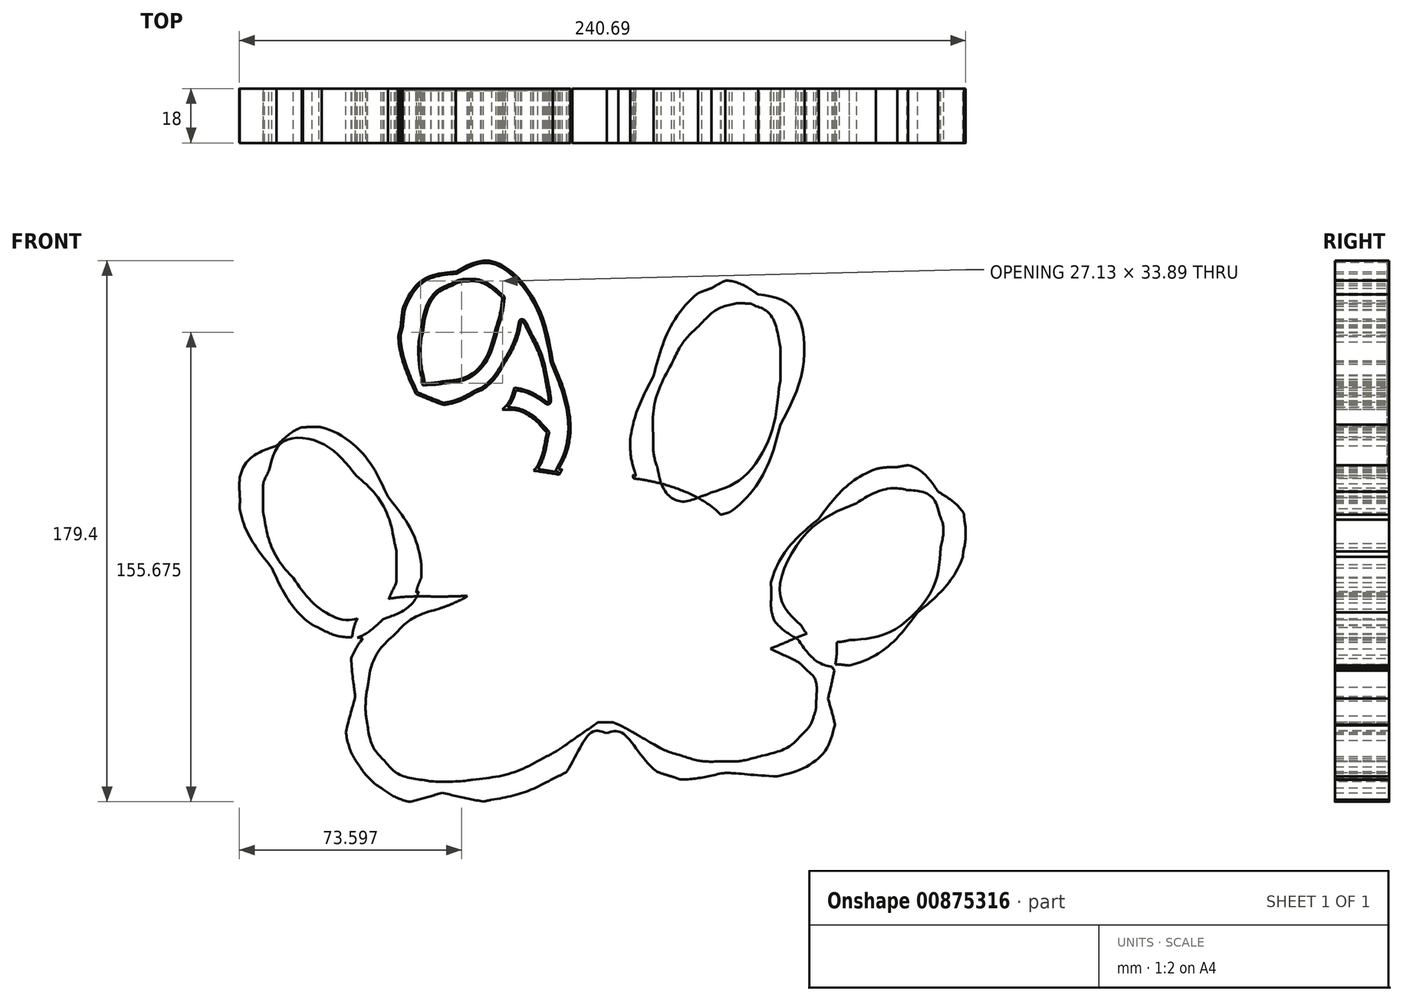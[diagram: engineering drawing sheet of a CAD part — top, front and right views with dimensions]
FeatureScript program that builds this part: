
annotation { "Feature Type Name" : "Feature", "Feature Type Description" : "" }
export const myFeature = defineFeature(function(context is Context, id is Id, definition is map)
    precondition{}
    {
        {
            var Q0;
            Q0=qCreatedBy(makeId("Front.planeOp"),FACE);
            var sketch = newSketch(context, id + "F0", { "sketchPlane" : qUnion([Q0])});
            skLineSegment(sketch, "E0", {"start": v(-80.3, -36.83) * mm, "end": v(-79.54, -35.55) * mm});
            skLineSegment(sketch, "E1", {"start": v(-79.54, -35.55) * mm, "end": v(-82.14, -35.4) * mm});
            skLineSegment(sketch, "E2", {"start": v(-13.99, 21.5) * mm, "end": v(-14.63, 20.22) * mm});
            skLineSegment(sketch, "E3", {"start": v(-14.63, 20.22) * mm, "end": v(-12.85, 20.36) * mm});
            skLineSegment(sketch, "E4", {"start": v(78.32, -44.34) * mm, "end": v(75.75, -44.48) * mm});
            skLineSegment(sketch, "E5", {"start": v(75.75, -44.48) * mm, "end": v(76.38, -45.72) * mm});
            skLineSegment(sketch, "E6", {"start": v(2.33, -71.3) * mm, "end": v(1.37, -70.89) * mm});
            skLineSegment(sketch, "E7", {"start": v(1.37, -70.89) * mm, "end": v(0.6, -71.36) * mm});
            skLineSegment(sketch, "E8", {"start": v(-18.9, 30.27) * mm, "end": v(-18.36, 32.47) * mm});
            skLineSegment(sketch, "E9", {"start": v(-18.36, 32.47) * mm, "end": v(-19.73, 33.87) * mm});
            skLineSegment(sketch, "E10", {"start": v(-59.45, 51.7) * mm, "end": v(-58.94, 48.84) * mm});
            skLineSegment(sketch, "E11", {"start": v(-58.94, 48.84) * mm, "end": v(-56.82, 48.98) * mm});
            skFitSpline(sketch, "E12", {"points": [v(-15.34, 34.63) * mm, v(-18.4, 39.06) * mm, v(-30.81, 48.02) * mm, v(-39.96, 41.9) * mm]});
            skFitSpline(sketch, "E13", {"points": [v(-39.96, 41.9) * mm, v(-49.1, 35.76) * mm, v(-49.72, 24.31) * mm, v(-47.56, 20.99) * mm]});
            skFitSpline(sketch, "E14", {"points": [v(-61.86, 45.3) * mm, v(-31.13, 42.45) * mm, v(-29.4, 77.45) * mm, v(-29.37, 77.9) * mm, v(-29.37, 77.9) * mm, v(-29.37, 77.91) * mm]});
            skFitSpline(sketch, "E15", {"points": [v(-48.61, 85.84) * mm, v(-60.56, 82.37) * mm, v(-67.65, 65.27) * mm, v(-61.86, 45.3) * mm]});
            skFitSpline(sketch, "E16", {"points": [v(-61.86, 45.3) * mm, v(-56.07, 25.33) * mm, v(-39.6, 10.07) * mm, v(-27.64, 13.53) * mm]});
            skFitSpline(sketch, "E17", {"points": [v(-27.64, 13.53) * mm, v(-15.69, 17) * mm, v(-10.7, 36) * mm, v(-16.48, 55.96) * mm]});
            skFitSpline(sketch, "E18", {"points": [v(-16.48, 55.96) * mm, v(-22.28, 75.93) * mm, v(-36.66, 89.3) * mm, v(-48.61, 85.84) * mm]});
            skFitSpline(sketch, "E19", {"points": [v(51.53, 78.32) * mm, v(39.92, 82.8) * mm, v(24.43, 70.73) * mm, v(16.93, 51.34) * mm]});
            skFitSpline(sketch, "E20", {"points": [v(16.93, 51.34) * mm, v(9.43, 31.95) * mm, v(12.76, 12.6) * mm, v(24.36, 8.1) * mm]});
            skFitSpline(sketch, "E21", {"points": [v(24.36, 8.1) * mm, v(35.97, 3.61) * mm, v(51.46, 15.7) * mm, v(58.96, 35.08) * mm]});
            skFitSpline(sketch, "E22", {"points": [v(58.96, 35.08) * mm, v(66.46, 54.47) * mm, v(63.13, 73.83) * mm, v(51.53, 78.32) * mm]});
            skFitSpline(sketch, "E23", {"points": [v(-108.03, 28.18) * mm, v(-118.63, 21.67) * mm, v(-119.33, 3.52) * mm, v(-109.59, -12.37) * mm]});
            skFitSpline(sketch, "E24", {"points": [v(-109.59, -12.37) * mm, v(-99.84, -28.26) * mm, v(-83.34, -35.86) * mm, v(-72.73, -29.35) * mm]});
            skFitSpline(sketch, "E25", {"points": [v(-72.73, -29.35) * mm, v(-62.12, -22.84) * mm, v(-61.42, -4.69) * mm, v(-71.17, 11.2) * mm]});
            skFitSpline(sketch, "E26", {"points": [v(-71.17, 11.2) * mm, v(-80.92, 27.09) * mm, v(-97.42, 34.69) * mm, v(-108.03, 28.18) * mm]});
            skFitSpline(sketch, "E27", {"points": [v(111.2, 12.89) * mm, v(102.17, 21.45) * mm, v(84.46, 17.41) * mm, v(71.64, 3.88) * mm]});
            skFitSpline(sketch, "E28", {"points": [v(71.64, 3.88) * mm, v(58.83, -9.66) * mm, v(55.77, -27.56) * mm, v(64.8, -36.12) * mm]});
            skFitSpline(sketch, "E29", {"points": [v(64.8, -36.12) * mm, v(73.84, -44.68) * mm, v(91.55, -40.64) * mm, v(104.37, -27.1) * mm]});
            skFitSpline(sketch, "E30", {"points": [v(104.37, -27.1) * mm, v(117.18, -13.57) * mm, v(120.24, 4.33) * mm, v(111.2, 12.89) * mm]});
            skFitSpline(sketch, "E31", {"points": [v(-4.8, 16.91) * mm, v(13.08, 16.91) * mm, v(40.29, 3.9) * mm, v(43.89, -20.36) * mm]});
            skFitSpline(sketch, "E32", {"points": [v(43.89, -20.36) * mm, v(46.93, -40.9) * mm, v(74.7, -32.91) * mm, v(74.7, -55.73) * mm]});
            skFitSpline(sketch, "E33", {"points": [v(74.7, -55.73) * mm, v(74.7, -78.55) * mm, v(43.89, -80.46) * mm, v(39.32, -80.46) * mm]});
            skFitSpline(sketch, "E34", {"points": [v(39.32, -80.46) * mm, v(18.78, -80.46) * mm, v(6.61, -67.14) * mm, v(1.29, -67.14) * mm]});
            skFitSpline(sketch, "E35", {"points": [v(1.29, -67.14) * mm, v(-4.04, -67.14) * mm, v(-17.73, -86.92) * mm, v(-53.1, -86.92) * mm]});
            skFitSpline(sketch, "E36", {"points": [v(-53.1, -86.92) * mm, v(-85.93, -86.92) * mm, v(-82.06, -55.39) * mm, v(-82, -54.97) * mm, v(-82, -54.97) * mm, v(-82, -54.97) * mm]});
            skFitSpline(sketch, "E37", {"points": [v(-82, -54.97) * mm, v(-82, -54.97) * mm, v(-82, -54.97) * mm, v(-82, -54.64) * mm, v(-81.47, -29.6) * mm, v(-54.24, -21.88) * mm]});
            skFitSpline(sketch, "E38", {"points": [v(-54.24, -21.88) * mm, v(-31.42, -15.42) * mm, v(-51.58, 16.91) * mm, v(-4.8, 16.91) * mm]});
            skFitSpline(sketch, "E39", {"points": [v(-57.5, -90.51) * mm, v(-63.49, -89.98) * mm, v(-69.01, -88.15) * mm, v(-73.42, -85.24) * mm]});
            skFitSpline(sketch, "E40", {"points": [v(-73.42, -85.24) * mm, v(-75.42, -83.92) * mm, v(-78.97, -80.36) * mm, v(-80.36, -78.28) * mm]});
            skFitSpline(sketch, "E41", {"points": [v(-80.36, -78.28) * mm, v(-82.64, -74.86) * mm, v(-84.2, -71) * mm, v(-85.22, -66.2) * mm]});
            skFitSpline(sketch, "E42", {"points": [v(-85.22, -66.2) * mm, v(-85.75, -63.7) * mm, v(-85.79, -63.17) * mm, v(-85.78, -58.3) * mm]});
            skFitSpline(sketch, "E43", {"points": [v(-85.78, -58.3) * mm, v(-85.77, -53.92) * mm, v(-85.7, -52.66) * mm, v(-85.32, -50.6) * mm]});
            skFitSpline(sketch, "E44", {"points": [v(-85.32, -50.6) * mm, v(-84.46, -45.94) * mm, v(-82.46, -40.44) * mm, v(-80.3, -36.83) * mm]});
            skFitSpline(sketch, "E45", {"points": [v(-82.14, -35.4) * mm, v(-86.47, -35.16) * mm, v(-90.16, -34.16) * mm, v(-94.14, -32.14) * mm]});
            skFitSpline(sketch, "E46", {"points": [v(-94.14, -32.14) * mm, v(-102.91, -27.68) * mm, v(-110.59, -19.5) * mm, v(-115.4, -9.51) * mm]});
            skFitSpline(sketch, "E47", {"points": [v(-115.4, -9.51) * mm, v(-118.68, -2.68) * mm, v(-120.14, 3.3) * mm, v(-120.15, 10.04) * mm]});
            skFitSpline(sketch, "E48", {"points": [v(-120.15, 10.04) * mm, v(-120.17, 18.1) * mm, v(-118, 24.09) * mm, v(-113.44, 28.63) * mm]});
            skFitSpline(sketch, "E49", {"points": [v(-113.44, 28.63) * mm, v(-109.65, 32.4) * mm, v(-105.08, 34.21) * mm, v(-99.36, 34.2) * mm]});
            skFitSpline(sketch, "E50", {"points": [v(-99.36, 34.2) * mm, v(-92.65, 34.2) * mm, v(-85.88, 31.5) * mm, v(-79.3, 26.2) * mm]});
            skFitSpline(sketch, "E51", {"points": [v(-79.3, 26.2) * mm, v(-65.67, 15.24) * mm, v(-57.9, -4.22) * mm, v(-61.35, -18.7) * mm]});
            skFitSpline(sketch, "E52", {"points": [v(-61.35, -18.7) * mm, v(-61.57, -19.63) * mm, v(-61.73, -20.41) * mm, v(-61.7, -20.44) * mm]});
            skFitSpline(sketch, "E53", {"points": [v(-61.7, -20.44) * mm, v(-61.67, -20.47) * mm, v(-61.04, -20.25) * mm, v(-60.3, -19.96) * mm]});
            skFitSpline(sketch, "E54", {"points": [v(-60.3, -19.96) * mm, v(-59.58, -19.66) * mm, v(-57.76, -19.02) * mm, v(-56.27, -18.54) * mm]});
            skFitSpline(sketch, "E55", {"points": [v(-56.27, -18.54) * mm, v(-52.77, -17.42) * mm, v(-50.94, -16.45) * mm, v(-49.43, -14.94) * mm]});
            skFitSpline(sketch, "E56", {"points": [v(-49.43, -14.94) * mm, v(-47.34, -12.83) * mm, v(-46.23, -10.59) * mm, v(-43.75, -3.42) * mm]});
            skFitSpline(sketch, "E57", {"points": [v(-43.75, -3.42) * mm, v(-41.73, 2.44) * mm, v(-39.65, 6.66) * mm, v(-37.51, 9.25) * mm]});
            skFitSpline(sketch, "E58", {"points": [v(-37.51, 9.25) * mm, v(-37.24, 9.58) * mm, v(-37.01, 9.93) * mm, v(-37.01, 10.02) * mm]});
            skFitSpline(sketch, "E59", {"points": [v(-37.01, 10.02) * mm, v(-37.01, 10.1) * mm, v(-37.4, 10.3) * mm, v(-37.87, 10.44) * mm]});
            skFitSpline(sketch, "E60", {"points": [v(-37.87, 10.44) * mm, v(-39.41, 10.9) * mm, v(-43.7, 13.2) * mm, v(-45.77, 14.68) * mm]});
            skFitSpline(sketch, "E61", {"points": [v(-45.77, 14.68) * mm, v(-48.16, 16.39) * mm, v(-53.03, 21.14) * mm, v(-55, 23.7) * mm]});
            skFitSpline(sketch, "E62", {"points": [v(-55, 23.7) * mm, v(-58.07, 27.7) * mm, v(-60.72, 32.12) * mm, v(-62.55, 36.28) * mm]});
            skFitSpline(sketch, "E63", {"points": [v(-62.55, 36.28) * mm, v(-67.27, 47) * mm, v(-68.77, 57.86) * mm, v(-66.9, 67.62) * mm]});
            skFitSpline(sketch, "E64", {"points": [v(-66.9, 67.62) * mm, v(-64.64, 79.28) * mm, v(-57.4, 87.89) * mm, v(-48.29, 89.77) * mm]});
            skFitSpline(sketch, "E65", {"points": [v(-48.29, 89.77) * mm, v(-32.27, 93.07) * mm, v(-14.8, 73.6) * mm, v(-10.94, 48.16) * mm]});
            skFitSpline(sketch, "E66", {"points": [v(-10.94, 48.16) * mm, v(-10.39, 44.56) * mm, v(-10.19, 38.26) * mm, v(-10.52, 34.91) * mm]});
            skFitSpline(sketch, "E67", {"points": [v(-10.52, 34.91) * mm, v(-11, 29.95) * mm, v(-12.35, 24.75) * mm, v(-13.99, 21.5) * mm]});
            skFitSpline(sketch, "E68", {"points": [v(-12.85, 20.36) * mm, v(-4.23, 21.06) * mm, v(2.6, 20.53) * mm, v(9.04, 18.67) * mm]});
            skFitSpline(sketch, "E69", {"points": [v(9.04, 18.67) * mm, v(10.05, 18.37) * mm, v(10.9, 18.17) * mm, v(10.94, 18.2) * mm]});
            skFitSpline(sketch, "E70", {"points": [v(10.94, 18.2) * mm, v(10.98, 18.24) * mm, v(10.78, 19.14) * mm, v(10.49, 20.19) * mm]});
            skFitSpline(sketch, "E71", {"points": [v(10.49, 20.19) * mm, v(9.54, 23.62) * mm, v(9.22, 26.4) * mm, v(9.23, 31.17) * mm]});
            skFitSpline(sketch, "E72", {"points": [v(9.23, 31.17) * mm, v(9.24, 35.88) * mm, v(9.55, 38.7) * mm, v(10.53, 43.13) * mm]});
            skFitSpline(sketch, "E73", {"points": [v(10.53, 43.13) * mm, v(14.22, 59.78) * mm, v(24.34, 74.51) * mm, v(36.12, 80.38) * mm]});
            skFitSpline(sketch, "E74", {"points": [v(36.12, 80.38) * mm, v(42.51, 83.56) * mm, v(48.6, 83.87) * mm, v(54.05, 81.28) * mm]});
            skFitSpline(sketch, "E75", {"points": [v(54.05, 81.28) * mm, v(62.44, 77.28) * mm, v(67.22, 66.82) * mm, v(66.69, 53.6) * mm]});
            skFitSpline(sketch, "E76", {"points": [v(66.69, 53.6) * mm, v(66.4, 46.63) * mm, v(65.03, 40.27) * mm, v(62.33, 33.42) * mm]});
            skFitSpline(sketch, "E77", {"points": [v(62.33, 33.42) * mm, v(56.76, 19.25) * mm, v(47.02, 8.36) * mm, v(36.65, 4.69) * mm]});
            skFitSpline(sketch, "E78", {"points": [v(36.65, 4.69) * mm, v(35.89, 4.42) * mm, v(35.22, 4.16) * mm, v(35.17, 4.12) * mm]});
            skFitSpline(sketch, "E79", {"points": [v(35.17, 4.12) * mm, v(35.12, 4.08) * mm, v(35.51, 3.6) * mm, v(36.04, 3.04) * mm]});
            skFitSpline(sketch, "E80", {"points": [v(36.04, 3.04) * mm, v(40.39, -1.52) * mm, v(43.64, -6.65) * mm, v(45.68, -12.17) * mm]});
            skFitSpline(sketch, "E81", {"points": [v(45.68, -12.17) * mm, v(46.4, -14.11) * mm, v(47.15, -17.13) * mm, v(47.85, -20.82) * mm]});
            skFitSpline(sketch, "E82", {"points": [v(47.85, -20.82) * mm, v(48.5, -24.23) * mm, v(50.62, -27.3) * mm, v(53.84, -29.46) * mm]});
            skFitSpline(sketch, "E83", {"points": [v(53.84, -29.46) * mm, v(55.55, -30.62) * mm, v(57.15, -31.48) * mm, v(57.15, -31.23) * mm]});
            skFitSpline(sketch, "E84", {"points": [v(57.15, -31.23) * mm, v(57.14, -31.14) * mm, v(56.96, -30.38) * mm, v(56.73, -29.53) * mm]});
            skFitSpline(sketch, "E85", {"points": [v(56.73, -29.53) * mm, v(56, -26.8) * mm, v(55.8, -24.67) * mm, v(55.94, -21.36) * mm]});
            skFitSpline(sketch, "E86", {"points": [v(55.94, -21.36) * mm, v(56.37, -11.53) * mm, v(61.38, -1.13) * mm, v(69.75, 7.27) * mm]});
            skFitSpline(sketch, "E87", {"points": [v(69.75, 7.27) * mm, v(74.2, 11.74) * mm, v(78.28, 14.73) * mm, v(83.28, 17.18) * mm]});
            skFitSpline(sketch, "E88", {"points": [v(83.28, 17.18) * mm, v(88.36, 19.66) * mm, v(92.77, 20.85) * mm, v(97.74, 21.07) * mm]});
            skFitSpline(sketch, "E89", {"points": [v(97.74, 21.07) * mm, v(109.43, 21.59) * mm, v(118, 14.83) * mm, v(119.85, 3.64) * mm]});
            skFitSpline(sketch, "E90", {"points": [v(119.85, 3.64) * mm, v(120.3, 0.95) * mm, v(120.13, -3.95) * mm, v(119.5, -6.94) * mm]});
            skFitSpline(sketch, "E91", {"points": [v(119.5, -6.94) * mm, v(115.44, -26.2) * mm, v(96.54, -43.36) * mm, v(78.32, -44.34) * mm]});
            skFitSpline(sketch, "E92", {"points": [v(76.38, -45.72) * mm, v(78.91, -50.73) * mm, v(79.14, -58.7) * mm, v(76.91, -64.6) * mm]});
            skFitSpline(sketch, "E93", {"points": [v(76.91, -64.6) * mm, v(73.76, -72.94) * mm, v(65.63, -79.14) * mm, v(53.8, -82.21) * mm]});
            skFitSpline(sketch, "E94", {"points": [v(53.8, -82.21) * mm, v(43.25, -84.95) * mm, v(33.23, -84.8) * mm, v(23.73, -81.76) * mm]});
            skFitSpline(sketch, "E95", {"points": [v(23.73, -81.76) * mm, v(18.72, -80.16) * mm, v(14.7, -78.27) * mm, v(7.59, -74.18) * mm]});
            skFitSpline(sketch, "E96", {"points": [v(7.59, -74.18) * mm, v(5.22, -72.82) * mm, v(2.85, -71.52) * mm, v(2.33, -71.3) * mm]});
            skFitSpline(sketch, "E97", {"points": [v(0.6, -71.36) * mm, v(0.17, -71.62) * mm, v(-1.62, -72.86) * mm, v(-3.38, -74.1) * mm]});
            skFitSpline(sketch, "E98", {"points": [v(-3.38, -74.1) * mm, v(-9.76, -78.62) * mm, v(-12.38, -80.25) * mm, v(-17.13, -82.62) * mm]});
            skFitSpline(sketch, "E99", {"points": [v(-17.13, -82.62) * mm, v(-23.28, -85.7) * mm, v(-29.8, -87.9) * mm, v(-36.8, -89.23) * mm]});
            skFitSpline(sketch, "E100", {"points": [v(-36.8, -89.23) * mm, v(-43.42, -90.5) * mm, v(-51.85, -91.01) * mm, v(-57.5, -90.51) * mm]});
            skFitSpline(sketch, "E101", {"points": [v(-43.01, -82.54) * mm, v(-34.4, -81.42) * mm, v(-26.81, -79.1) * mm, v(-19.83, -75.5) * mm]});
            skFitSpline(sketch, "E102", {"points": [v(-19.83, -75.5) * mm, v(-16.28, -73.67) * mm, v(-14.03, -72.3) * mm, v(-10, -69.48) * mm]});
            skFitSpline(sketch, "E103", {"points": [v(-10, -69.48) * mm, v(-1.6, -63.62) * mm, v(-1.46, -63.54) * mm, v(1.42, -63.53) * mm]});
            skFitSpline(sketch, "E104", {"points": [v(1.42, -63.53) * mm, v(3.29, -63.53) * mm, v(3.59, -63.59) * mm, v(5.16, -64.28) * mm]});
            skFitSpline(sketch, "E105", {"points": [v(5.16, -64.28) * mm, v(6.1, -64.7) * mm, v(8.98, -66.25) * mm, v(11.56, -67.73) * mm]});
            skFitSpline(sketch, "E106", {"points": [v(11.56, -67.73) * mm, v(18.75, -71.84) * mm, v(21.95, -73.33) * mm, v(26.83, -74.8) * mm]});
            skFitSpline(sketch, "E107", {"points": [v(26.83, -74.8) * mm, v(31.12, -76.1) * mm, v(34.2, -76.54) * mm, v(39.1, -76.53) * mm]});
            skFitSpline(sketch, "E108", {"points": [v(39.1, -76.53) * mm, v(44, -76.52) * mm, v(47.2, -76.1) * mm, v(52.03, -74.83) * mm]});
            skFitSpline(sketch, "E109", {"points": [v(52.03, -74.83) * mm, v(58.45, -73.14) * mm, v(62.73, -70.91) * mm, v(66.12, -67.48) * mm]});
            skFitSpline(sketch, "E110", {"points": [v(66.12, -67.48) * mm, v(68.22, -65.36) * mm, v(69.11, -63.95) * mm, v(70.02, -61.34) * mm]});
            skFitSpline(sketch, "E111", {"points": [v(70.02, -61.34) * mm, v(70.6, -59.68) * mm, v(70.69, -59.12) * mm, v(70.77, -56.48) * mm]});
            skFitSpline(sketch, "E112", {"points": [v(70.77, -56.48) * mm, v(70.92, -51.44) * mm, v(69.97, -48.54) * mm, v(67.33, -45.93) * mm]});
            skFitSpline(sketch, "E113", {"points": [v(67.33, -45.93) * mm, v(65.57, -44.2) * mm, v(63.76, -43.02) * mm, v(60.14, -41.28) * mm]});
            skFitSpline(sketch, "E114", {"points": [v(60.14, -41.28) * mm, v(53.37, -38.01) * mm, v(52.03, -37.32) * mm, v(50.1, -36.07) * mm]});
            skFitSpline(sketch, "E115", {"points": [v(50.1, -36.07) * mm, v(47.73, -34.54) * mm, v(44.18, -31.06) * mm, v(43.1, -29.21) * mm]});
            skFitSpline(sketch, "E116", {"points": [v(43.1, -29.21) * mm, v(41.65, -26.76) * mm, v(40.9, -24.61) * mm, v(40.14, -20.85) * mm]});
            skFitSpline(sketch, "E117", {"points": [v(40.14, -20.85) * mm, v(39.27, -16.55) * mm, v(38.72, -14.8) * mm, v(37.27, -11.75) * mm]});
            skFitSpline(sketch, "E118", {"points": [v(37.27, -11.75) * mm, v(31.32, 0.75) * mm, v(16.2, 10.68) * mm, v(-0.18, 12.83) * mm]});
            skFitSpline(sketch, "E119", {"points": [v(-0.18, 12.83) * mm, v(-2.73, 13.16) * mm, v(-11.79, 12.96) * mm, v(-14.8, 12.5) * mm]});
            skFitSpline(sketch, "E120", {"points": [v(-14.8, 12.5) * mm, v(-22.25, 11.38) * mm, v(-27.34, 9.16) * mm, v(-30.63, 5.6) * mm]});
            skFitSpline(sketch, "E121", {"points": [v(-30.63, 5.6) * mm, v(-33.05, 3) * mm, v(-34.48, 0.23) * mm, v(-36.6, -5.88) * mm]});
            skFitSpline(sketch, "E122", {"points": [v(-36.6, -5.88) * mm, v(-38.33, -10.9) * mm, v(-38.97, -12.5) * mm, v(-40.23, -14.95) * mm]});
            skFitSpline(sketch, "E123", {"points": [v(-40.23, -14.95) * mm, v(-42.25, -18.89) * mm, v(-45.4, -22.07) * mm, v(-49.04, -23.87) * mm]});
            skFitSpline(sketch, "E124", {"points": [v(-49.04, -23.87) * mm, v(-50, -24.34) * mm, v(-52.41, -25.27) * mm, v(-54.4, -25.93) * mm]});
            skFitSpline(sketch, "E125", {"points": [v(-54.4, -25.93) * mm, v(-60.74, -28.03) * mm, v(-64.91, -30.47) * mm, v(-68.83, -34.38) * mm]});
            skFitSpline(sketch, "E126", {"points": [v(-68.83, -34.38) * mm, v(-73.53, -39.07) * mm, v(-76.62, -45.06) * mm, v(-77.83, -51.88) * mm]});
            skFitSpline(sketch, "E127", {"points": [v(-77.83, -51.88) * mm, v(-78.37, -54.87) * mm, v(-78.48, -60.92) * mm, v(-78.04, -63.42) * mm]});
            skFitSpline(sketch, "E128", {"points": [v(-78.04, -63.42) * mm, v(-77.09, -68.93) * mm, v(-75.28, -73) * mm, v(-72.4, -76.13) * mm]});
            skFitSpline(sketch, "E129", {"points": [v(-72.4, -76.13) * mm, v(-69.14, -79.66) * mm, v(-64.81, -81.78) * mm, v(-58.9, -82.74) * mm]});
            skFitSpline(sketch, "E130", {"points": [v(-58.9, -82.74) * mm, v(-56.34, -83.15) * mm, v(-46.77, -83.03) * mm, v(-43.01, -82.54) * mm]});
            skFitSpline(sketch, "E131", {"points": [v(81.77, -36.29) * mm, v(95.46, -33.5) * mm, v(109.23, -19.52) * mm, v(112.01, -5.6) * mm]});
            skFitSpline(sketch, "E132", {"points": [v(112.01, -5.6) * mm, v(112.89, -1.21) * mm, v(112.78, 2.1) * mm, v(111.65, 5.28) * mm]});
            skFitSpline(sketch, "E133", {"points": [v(111.65, 5.28) * mm, v(109.95, 10.08) * mm, v(106.46, 12.71) * mm, v(100.83, 13.46) * mm]});
            skFitSpline(sketch, "E134", {"points": [v(100.83, 13.46) * mm, v(96.24, 14.07) * mm, v(89.76, 12.37) * mm, v(84.22, 9.11) * mm]});
            skFitSpline(sketch, "E135", {"points": [v(84.22, 9.11) * mm, v(67.94, -0.47) * mm, v(58.74, -20.77) * mm, v(65.83, -31.44) * mm]});
            skFitSpline(sketch, "E136", {"points": [v(65.83, -31.44) * mm, v(67.46, -33.9) * mm, v(69.91, -35.56) * mm, v(73.03, -36.32) * mm]});
            skFitSpline(sketch, "E137", {"points": [v(73.03, -36.32) * mm, v(75.23, -36.86) * mm, v(79.02, -36.85) * mm, v(81.77, -36.29) * mm]});
            skFitSpline(sketch, "E138", {"points": [v(-77.2, -27.2) * mm, v(-74.1, -26.18) * mm, v(-71.65, -24) * mm, v(-70.12, -20.87) * mm]});
            skFitSpline(sketch, "E139", {"points": [v(-70.12, -20.87) * mm, v(-68.57, -17.72) * mm, v(-68.31, -16.35) * mm, v(-68.31, -11.21) * mm]});
            skFitSpline(sketch, "E140", {"points": [v(-68.31, -11.21) * mm, v(-68.31, -7.05) * mm, v(-68.35, -6.55) * mm, v(-68.9, -4.19) * mm]});
            skFitSpline(sketch, "E141", {"points": [v(-68.9, -4.19) * mm, v(-70.9, 4.3) * mm, v(-75.5, 12.4) * mm, v(-81.6, 18.17) * mm]});
            skFitSpline(sketch, "E142", {"points": [v(-81.6, 18.17) * mm, v(-92.85, 28.84) * mm, v(-105.76, 29.56) * mm, v(-110.57, 19.8) * mm]});
            skFitSpline(sketch, "E143", {"points": [v(-110.57, 19.8) * mm, v(-112.2, 16.5) * mm, v(-112.47, 15.12) * mm, v(-112.47, 10.14) * mm]});
            skFitSpline(sketch, "E144", {"points": [v(-112.47, 10.14) * mm, v(-112.48, 6.5) * mm, v(-112.4, 5.54) * mm, v(-112, 3.63) * mm]});
            skFitSpline(sketch, "E145", {"points": [v(-112, 3.63) * mm, v(-110.52, -3.22) * mm, v(-107.06, -10.3) * mm, v(-102.53, -15.7) * mm]});
            skFitSpline(sketch, "E146", {"points": [v(-102.53, -15.7) * mm, v(-94.66, -25.1) * mm, v(-84.63, -29.65) * mm, v(-77.2, -27.2) * mm]});
            skFitSpline(sketch, "E147", {"points": [v(32.92, 11.45) * mm, v(33.62, 11.63) * mm, v(34.98, 12.14) * mm, v(35.93, 12.59) * mm]});
            skFitSpline(sketch, "E148", {"points": [v(35.93, 12.59) * mm, v(46.38, 17.47) * mm, v(55.67, 31.79) * mm, v(58.47, 47.32) * mm]});
            skFitSpline(sketch, "E149", {"points": [v(58.47, 47.32) * mm, v(58.9, 49.71) * mm, v(58.96, 50.75) * mm, v(58.96, 55.3) * mm]});
            skFitSpline(sketch, "E150", {"points": [v(58.96, 55.3) * mm, v(58.96, 59.84) * mm, v(58.9, 60.8) * mm, v(58.5, 62.56) * mm]});
            skFitSpline(sketch, "E151", {"points": [v(58.5, 62.56) * mm, v(57.16, 68.65) * mm, v(54.58, 72.63) * mm, v(50.83, 74.43) * mm]});
            skFitSpline(sketch, "E152", {"points": [v(50.83, 74.43) * mm, v(49.28, 75.18) * mm, v(48.97, 75.25) * mm, v(46.9, 75.33) * mm]});
            skFitSpline(sketch, "E153", {"points": [v(46.9, 75.33) * mm, v(45.04, 75.4) * mm, v(44.34, 75.34) * mm, v(42.94, 74.96) * mm]});
            skFitSpline(sketch, "E154", {"points": [v(42.94, 74.96) * mm, v(39.18, 73.93) * mm, v(35.8, 71.75) * mm, v(31.83, 67.8) * mm]});
            skFitSpline(sketch, "E155", {"points": [v(31.83, 67.8) * mm, v(27.92, 63.9) * mm, v(25.46, 60.46) * mm, v(22.81, 55.18) * mm]});
            skFitSpline(sketch, "E156", {"points": [v(22.81, 55.18) * mm, v(18.81, 47.22) * mm, v(16.8, 39.15) * mm, v(16.8, 31.14) * mm]});
            skFitSpline(sketch, "E157", {"points": [v(16.8, 31.14) * mm, v(16.8, 27.09) * mm, v(17.2, 24.01) * mm, v(18.12, 21.15) * mm]});
            skFitSpline(sketch, "E158", {"points": [v(18.12, 21.15) * mm, v(20.68, 13.12) * mm, v(25.92, 9.68) * mm, v(32.92, 11.45) * mm]});
            skFitSpline(sketch, "E159", {"points": [v(-27.83, 17.48) * mm, v(-23.74, 19.08) * mm, v(-20.56, 23.64) * mm, v(-18.9, 30.27) * mm]});
            skFitSpline(sketch, "E160", {"points": [v(-19.73, 33.87) * mm, v(-23.13, 37.32) * mm, v(-28.16, 39.82) * mm, v(-32.23, 40.08) * mm]});
            skFitSpline(sketch, "E161", {"points": [v(-32.23, 40.08) * mm, v(-33.85, 40.18) * mm, v(-34.43, 40.13) * mm, v(-35.65, 39.75) * mm]});
            skFitSpline(sketch, "E162", {"points": [v(-35.65, 39.75) * mm, v(-38.43, 38.9) * mm, v(-41.3, 36.2) * mm, v(-43, 32.85) * mm]});
            skFitSpline(sketch, "E163", {"points": [v(-43, 32.85) * mm, v(-44.33, 30.24) * mm, v(-44.78, 28.14) * mm, v(-44.72, 24.8) * mm]});
            skFitSpline(sketch, "E164", {"points": [v(-44.72, 24.8) * mm, v(-44.7, 23.75) * mm, v(-44.63, 23.57) * mm, v(-43.9, 22.89) * mm]});
            skFitSpline(sketch, "E165", {"points": [v(-43.9, 22.89) * mm, v(-41.44, 20.56) * mm, v(-36.82, 17.87) * mm, v(-34.13, 17.2) * mm]});
            skFitSpline(sketch, "E166", {"points": [v(-34.13, 17.2) * mm, v(-32.33, 16.75) * mm, v(-29.35, 16.88) * mm, v(-27.83, 17.48) * mm]});
            skFitSpline(sketch, "E167", {"points": [v(-51.32, 32.4) * mm, v(-51.3, 33.07) * mm, v(-49.87, 36.3) * mm, v(-48.83, 37.96) * mm]});
            skFitSpline(sketch, "E168", {"points": [v(-48.83, 37.96) * mm, v(-45.93, 42.62) * mm, v(-41.74, 45.93) * mm, v(-37.12, 47.21) * mm]});
            skFitSpline(sketch, "E169", {"points": [v(-37.12, 47.21) * mm, v(-34.98, 47.8) * mm, v(-31.35, 47.85) * mm, v(-28.8, 47.3) * mm]});
            skFitSpline(sketch, "E170", {"points": [v(-28.8, 47.3) * mm, v(-25.82, 46.67) * mm, v(-21.8, 44.92) * mm, v(-19.12, 43.08) * mm]});
            skFitSpline(sketch, "E171", {"points": [v(-19.12, 43.08) * mm, v(-18.6, 42.73) * mm, v(-18.13, 42.51) * mm, v(-18.06, 42.58) * mm]});
            skFitSpline(sketch, "E172", {"points": [v(-18.06, 42.58) * mm, v(-17.86, 42.79) * mm, v(-18.4, 47.2) * mm, v(-18.97, 50.08) * mm]});
            skFitSpline(sketch, "E173", {"points": [v(-18.97, 50.08) * mm, v(-19.99, 55.14) * mm, v(-21.64, 60) * mm, v(-23.78, 64.29) * mm]});
            skFitSpline(sketch, "E174", {"points": [v(-23.78, 64.29) * mm, v(-25.1, 66.93) * mm, v(-26.54, 69.4) * mm, v(-26.76, 69.4) * mm]});
            skFitSpline(sketch, "E175", {"points": [v(-26.76, 69.4) * mm, v(-26.84, 69.4) * mm, v(-27.03, 68.84) * mm, v(-27.18, 68.17) * mm]});
            skFitSpline(sketch, "E176", {"points": [v(-27.18, 68.17) * mm, v(-27.94, 64.8) * mm, v(-30.2, 59.32) * mm, v(-32.22, 56) * mm]});
            skFitSpline(sketch, "E177", {"points": [v(-32.22, 56) * mm, v(-35.26, 50.99) * mm, v(-39.67, 46.81) * mm, v(-44.45, 44.43) * mm]});
            skFitSpline(sketch, "E178", {"points": [v(-44.45, 44.43) * mm, v(-47.21, 43.04) * mm, v(-51.55, 41.84) * mm, v(-54.9, 41.52) * mm]});
            skFitSpline(sketch, "E179", {"points": [v(-54.9, 41.52) * mm, v(-56.71, 41.34) * mm, v(-56.68, 41.6) * mm, v(-55.25, 38.5) * mm]});
            skFitSpline(sketch, "E180", {"points": [v(-55.25, 38.5) * mm, v(-54.12, 36.08) * mm, v(-51.79, 32.03) * mm, v(-51.51, 32.03) * mm]});
            skFitSpline(sketch, "E181", {"points": [v(-51.51, 32.03) * mm, v(-51.4, 32.03) * mm, v(-51.32, 32.2) * mm, v(-51.32, 32.4) * mm]});
            skFitSpline(sketch, "E182", {"points": [v(-53.09, 49.45) * mm, v(-44.68, 51.18) * mm, v(-38.62, 57.32) * mm, v(-35.3, 67.43) * mm]});
            skFitSpline(sketch, "E183", {"points": [v(-35.3, 67.43) * mm, v(-34.52, 69.85) * mm, v(-33.62, 73.83) * mm, v(-33.3, 76.27) * mm]});
            skFitSpline(sketch, "E184", {"points": [v(-33.3, 76.27) * mm, v(-33.18, 77.25) * mm, v(-33.2, 77.28) * mm, v(-34.2, 78.1) * mm]});
            skFitSpline(sketch, "E185", {"points": [v(-34.2, 78.1) * mm, v(-37.55, 80.87) * mm, v(-41.63, 82.63) * mm, v(-44.7, 82.63) * mm]});
            skFitSpline(sketch, "E186", {"points": [v(-44.7, 82.63) * mm, v(-46.14, 82.63) * mm, v(-48.16, 82.09) * mm, v(-49.77, 81.26) * mm]});
            skFitSpline(sketch, "E187", {"points": [v(-49.77, 81.26) * mm, v(-54.63, 78.79) * mm, v(-58.05, 73.35) * mm, v(-59.58, 65.66) * mm]});
            skFitSpline(sketch, "E188", {"points": [v(-59.58, 65.66) * mm, v(-60.2, 62.59) * mm, v(-60.13, 55.46) * mm, v(-59.45, 51.7) * mm]});
            skFitSpline(sketch, "E189", {"points": [v(-56.82, 48.98) * mm, v(-55.65, 49.05) * mm, v(-53.97, 49.27) * mm, v(-53.09, 49.45) * mm]});
            skSolve(sketch);
        }
        {
            var Q0;
            Q0=makeQuery(id+"F0.imprint","IMPRINT",FACE,{"disambiguationData":[TD([[makeQuery(id+"F0.imprint","IMPRINT",EDGE,{"derivedFrom":sQuery(id+"F0.wireOp",EDGE,"E0")}),-1.0]])]});
            var Q1;
            Q1=makeQuery(id+"F0.imprint","IMPRINT",FACE,{"disambiguationData":[TD([[makeQuery(id+"F0.imprint","IMPRINT",EDGE,{"derivedFrom":sQuery(id+"F0.wireOp",EDGE,"E8")}),-1.0]])]});
            var Q2;
            Q2=makeQuery(id+"F0.imprint","IMPRINT",FACE,{"disambiguationData":[TD([[makeQuery(id+"F0.imprint","IMPRINT",EDGE,{"derivedFrom":sQuery(id+"F0.wireOp",EDGE,"E23")}),1.0]])]});
            var Q3;
            Q3=makeQuery(id+"F0.imprint","IMPRINT",FACE,{"disambiguationData":[TD([[makeQuery(id+"F0.imprint","IMPRINT",EDGE,{"derivedFrom":sQuery(id+"F0.wireOp",EDGE,"E31")}),-1.0]])]});
            var Q4;
            Q4=makeQuery(id+"F0.imprint","IMPRINT",FACE,{"disambiguationData":[TD([[makeQuery(id+"F0.imprint","IMPRINT",EDGE,{"derivedFrom":sQuery(id+"F0.wireOp",EDGE,"E19")}),1.0]])]});
            var Q5;
            Q5=makeQuery(id+"F0.imprint","IMPRINT",FACE,{"disambiguationData":[TD([[makeQuery(id+"F0.imprint","IMPRINT",EDGE,{"derivedFrom":sQuery(id+"F0.wireOp",EDGE,"E27")}),1.0]])]});
            extrude(context, id + "F1", {"entities" : qUnion([Q0, Q1, Q2, Q3, Q4, Q5]), "depth" : 18 * mm, "offsetDistance" : 25 * mm});
        }
        {
            var Q0;
            Q0=makeQuery(id+"F1.opExtrude","CAP_FACE",FACE,{"disambiguationData":[OSD([sQuery(id+"F0.wireOp",EDGE,"E0"),sQuery(id+"F0.wireOp",EDGE,"E1"),sQuery(id+"F0.wireOp",EDGE,"E2"),sQuery(id+"F0.wireOp",EDGE,"E3"),sQuery(id+"F0.wireOp",EDGE,"E4"),sQuery(id+"F0.wireOp",EDGE,"E5"),sQuery(id+"F0.wireOp",EDGE,"E6"),sQuery(id+"F0.wireOp",EDGE,"E7"),sQuery(id+"F0.wireOp",EDGE,"E8"),sQuery(id+"F0.wireOp",EDGE,"E9"),sQuery(id+"F0.wireOp",EDGE,"E10"),sQuery(id+"F0.wireOp",EDGE,"E11"),sQuery(id+"F0.wireOp",EDGE,"E39"),sQuery(id+"F0.wireOp",EDGE,"E40"),sQuery(id+"F0.wireOp",EDGE,"E41"),sQuery(id+"F0.wireOp",EDGE,"E42"),sQuery(id+"F0.wireOp",EDGE,"E43"),sQuery(id+"F0.wireOp",EDGE,"E44"),sQuery(id+"F0.wireOp",EDGE,"E45"),sQuery(id+"F0.wireOp",EDGE,"E46"),sQuery(id+"F0.wireOp",EDGE,"E47"),sQuery(id+"F0.wireOp",EDGE,"E48"),sQuery(id+"F0.wireOp",EDGE,"E49"),sQuery(id+"F0.wireOp",EDGE,"E50"),sQuery(id+"F0.wireOp",EDGE,"E51"),sQuery(id+"F0.wireOp",EDGE,"E52"),sQuery(id+"F0.wireOp",EDGE,"E53"),sQuery(id+"F0.wireOp",EDGE,"E54"),sQuery(id+"F0.wireOp",EDGE,"E55"),sQuery(id+"F0.wireOp",EDGE,"E56"),sQuery(id+"F0.wireOp",EDGE,"E57"),sQuery(id+"F0.wireOp",EDGE,"E58"),sQuery(id+"F0.wireOp",EDGE,"E59"),sQuery(id+"F0.wireOp",EDGE,"E60"),sQuery(id+"F0.wireOp",EDGE,"E61"),sQuery(id+"F0.wireOp",EDGE,"E62"),sQuery(id+"F0.wireOp",EDGE,"E63"),sQuery(id+"F0.wireOp",EDGE,"E64"),sQuery(id+"F0.wireOp",EDGE,"E65"),sQuery(id+"F0.wireOp",EDGE,"E66"),sQuery(id+"F0.wireOp",EDGE,"E67"),sQuery(id+"F0.wireOp",EDGE,"E68"),sQuery(id+"F0.wireOp",EDGE,"E69"),sQuery(id+"F0.wireOp",EDGE,"E70"),sQuery(id+"F0.wireOp",EDGE,"E71"),sQuery(id+"F0.wireOp",EDGE,"E72"),sQuery(id+"F0.wireOp",EDGE,"E73"),sQuery(id+"F0.wireOp",EDGE,"E74"),sQuery(id+"F0.wireOp",EDGE,"E75"),sQuery(id+"F0.wireOp",EDGE,"E76"),sQuery(id+"F0.wireOp",EDGE,"E77"),sQuery(id+"F0.wireOp",EDGE,"E78"),sQuery(id+"F0.wireOp",EDGE,"E79"),sQuery(id+"F0.wireOp",EDGE,"E80"),sQuery(id+"F0.wireOp",EDGE,"E81"),sQuery(id+"F0.wireOp",EDGE,"E82"),sQuery(id+"F0.wireOp",EDGE,"E83"),sQuery(id+"F0.wireOp",EDGE,"E84"),sQuery(id+"F0.wireOp",EDGE,"E85"),sQuery(id+"F0.wireOp",EDGE,"E86"),sQuery(id+"F0.wireOp",EDGE,"E87"),sQuery(id+"F0.wireOp",EDGE,"E88"),sQuery(id+"F0.wireOp",EDGE,"E89"),sQuery(id+"F0.wireOp",EDGE,"E90"),sQuery(id+"F0.wireOp",EDGE,"E91"),sQuery(id+"F0.wireOp",EDGE,"E92"),sQuery(id+"F0.wireOp",EDGE,"E93"),sQuery(id+"F0.wireOp",EDGE,"E94"),sQuery(id+"F0.wireOp",EDGE,"E95"),sQuery(id+"F0.wireOp",EDGE,"E96"),sQuery(id+"F0.wireOp",EDGE,"E97"),sQuery(id+"F0.wireOp",EDGE,"E98"),sQuery(id+"F0.wireOp",EDGE,"E99"),sQuery(id+"F0.wireOp",EDGE,"E100"),sQuery(id+"F0.wireOp",EDGE,"E101"),sQuery(id+"F0.wireOp",EDGE,"E102"),sQuery(id+"F0.wireOp",EDGE,"E103"),sQuery(id+"F0.wireOp",EDGE,"E104"),sQuery(id+"F0.wireOp",EDGE,"E105"),sQuery(id+"F0.wireOp",EDGE,"E106"),sQuery(id+"F0.wireOp",EDGE,"E107"),sQuery(id+"F0.wireOp",EDGE,"E108"),sQuery(id+"F0.wireOp",EDGE,"E109"),sQuery(id+"F0.wireOp",EDGE,"E110"),sQuery(id+"F0.wireOp",EDGE,"E111"),sQuery(id+"F0.wireOp",EDGE,"E112"),sQuery(id+"F0.wireOp",EDGE,"E113"),sQuery(id+"F0.wireOp",EDGE,"E114"),sQuery(id+"F0.wireOp",EDGE,"E115"),sQuery(id+"F0.wireOp",EDGE,"E116"),sQuery(id+"F0.wireOp",EDGE,"E117"),sQuery(id+"F0.wireOp",EDGE,"E118"),sQuery(id+"F0.wireOp",EDGE,"E119"),sQuery(id+"F0.wireOp",EDGE,"E120"),sQuery(id+"F0.wireOp",EDGE,"E121"),sQuery(id+"F0.wireOp",EDGE,"E122"),sQuery(id+"F0.wireOp",EDGE,"E123"),sQuery(id+"F0.wireOp",EDGE,"E124"),sQuery(id+"F0.wireOp",EDGE,"E125"),sQuery(id+"F0.wireOp",EDGE,"E126"),sQuery(id+"F0.wireOp",EDGE,"E127"),sQuery(id+"F0.wireOp",EDGE,"E128"),sQuery(id+"F0.wireOp",EDGE,"E129"),sQuery(id+"F0.wireOp",EDGE,"E130"),sQuery(id+"F0.wireOp",EDGE,"E131"),sQuery(id+"F0.wireOp",EDGE,"E132"),sQuery(id+"F0.wireOp",EDGE,"E133"),sQuery(id+"F0.wireOp",EDGE,"E134"),sQuery(id+"F0.wireOp",EDGE,"E135"),sQuery(id+"F0.wireOp",EDGE,"E136"),sQuery(id+"F0.wireOp",EDGE,"E137"),sQuery(id+"F0.wireOp",EDGE,"E138"),sQuery(id+"F0.wireOp",EDGE,"E139"),sQuery(id+"F0.wireOp",EDGE,"E140"),sQuery(id+"F0.wireOp",EDGE,"E141"),sQuery(id+"F0.wireOp",EDGE,"E142"),sQuery(id+"F0.wireOp",EDGE,"E143"),sQuery(id+"F0.wireOp",EDGE,"E144"),sQuery(id+"F0.wireOp",EDGE,"E145"),sQuery(id+"F0.wireOp",EDGE,"E146"),sQuery(id+"F0.wireOp",EDGE,"E147"),sQuery(id+"F0.wireOp",EDGE,"E148"),sQuery(id+"F0.wireOp",EDGE,"E149"),sQuery(id+"F0.wireOp",EDGE,"E150"),sQuery(id+"F0.wireOp",EDGE,"E151"),sQuery(id+"F0.wireOp",EDGE,"E152"),sQuery(id+"F0.wireOp",EDGE,"E153"),sQuery(id+"F0.wireOp",EDGE,"E154"),sQuery(id+"F0.wireOp",EDGE,"E155"),sQuery(id+"F0.wireOp",EDGE,"E156"),sQuery(id+"F0.wireOp",EDGE,"E157"),sQuery(id+"F0.wireOp",EDGE,"E158"),sQuery(id+"F0.wireOp",EDGE,"E159"),sQuery(id+"F0.wireOp",EDGE,"E160"),sQuery(id+"F0.wireOp",EDGE,"E161"),sQuery(id+"F0.wireOp",EDGE,"E162"),sQuery(id+"F0.wireOp",EDGE,"E163"),sQuery(id+"F0.wireOp",EDGE,"E164"),sQuery(id+"F0.wireOp",EDGE,"E165"),sQuery(id+"F0.wireOp",EDGE,"E166"),sQuery(id+"F0.wireOp",EDGE,"E167"),sQuery(id+"F0.wireOp",EDGE,"E168"),sQuery(id+"F0.wireOp",EDGE,"E169"),sQuery(id+"F0.wireOp",EDGE,"E170"),sQuery(id+"F0.wireOp",EDGE,"E171"),sQuery(id+"F0.wireOp",EDGE,"E172"),sQuery(id+"F0.wireOp",EDGE,"E173"),sQuery(id+"F0.wireOp",EDGE,"E174"),sQuery(id+"F0.wireOp",EDGE,"E175"),sQuery(id+"F0.wireOp",EDGE,"E176"),sQuery(id+"F0.wireOp",EDGE,"E177"),sQuery(id+"F0.wireOp",EDGE,"E178"),sQuery(id+"F0.wireOp",EDGE,"E179"),sQuery(id+"F0.wireOp",EDGE,"E180"),sQuery(id+"F0.wireOp",EDGE,"E181"),sQuery(id+"F0.wireOp",EDGE,"E182"),sQuery(id+"F0.wireOp",EDGE,"E183"),sQuery(id+"F0.wireOp",EDGE,"E184"),sQuery(id+"F0.wireOp",EDGE,"E185"),sQuery(id+"F0.wireOp",EDGE,"E186"),sQuery(id+"F0.wireOp",EDGE,"E187"),sQuery(id+"F0.wireOp",EDGE,"E188"),sQuery(id+"F0.wireOp",EDGE,"E189")])],"isStart":false});
            shell(context, id + "F2", {"entities" : qUnion([Q0]), "thickness" : 0.7 * mm});
        }
    });
